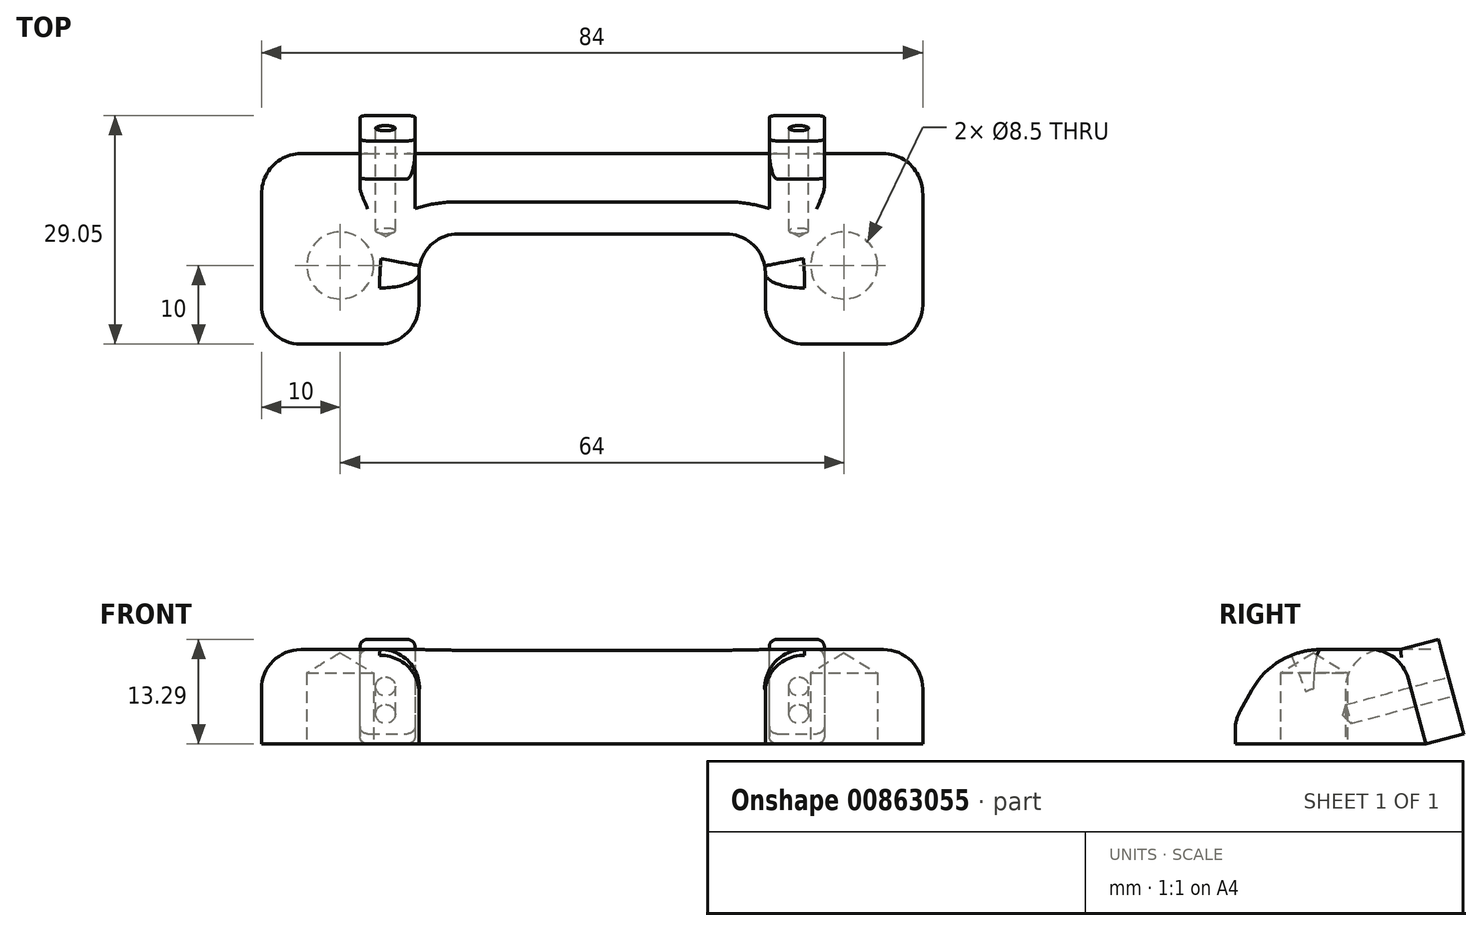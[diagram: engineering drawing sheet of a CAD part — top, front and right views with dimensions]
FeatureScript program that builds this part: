
annotation { "Feature Type Name" : "Feature", "Feature Type Description" : "" }
export const myFeature = defineFeature(function(context is Context, id is Id, definition is map)
    precondition{}
    {
        {
            var Q0;
            Q0=qCreatedBy(makeId("Top.planeOp"),FACE);
            var sketch = newSketch(context, id + "F0", { "sketchPlane" : qUnion([Q0])});
            skPoint(sketch, "E0", {"position": v(-32, 0) * mm});
            skPoint(sketch, "E1", {"position": v(32, 0) * mm});
            skLineSegment(sketch, "E2.bottom", {"start": v(-42, 8) * mm, "end": v(42, 8) * mm});
            skLineSegment(sketch, "E2.top", {"start": v(-42, -10) * mm, "end": v(42, -10) * mm});
            skLineSegment(sketch, "E2.left", {"start": v(-42, 8) * mm, "end": v(-42, -10) * mm});
            skLineSegment(sketch, "E2.right", {"start": v(42, 8) * mm, "end": v(42, -10) * mm});
            skLineSegment(sketch, "E3.top", {"start": v(-42, 11) * mm, "end": v(42, 11) * mm});
            skLineSegment(sketch, "E3.left", {"start": v(-42, 8) * mm, "end": v(-42, 11) * mm});
            skLineSegment(sketch, "E3.right", {"start": v(42, 8) * mm, "end": v(42, 11) * mm});
            skSolve(sketch);
        }
        {
            var Q0;
            Q0=makeQuery(id+"F0.imprint","IMPRINT",FACE,{"disambiguationData":[TD([[makeQuery(id+"F0.imprint","IMPRINT",EDGE,{"derivedFrom":sQuery(id+"F0.wireOp",EDGE,"MXNtf99J-OJbA-ETAj-UOV1-NQ5tLVOZiuJ5")}),-1.0]])]});
            var Q1;
            Q1=makeQuery(id+"F0.imprint","IMPRINT",FACE,{"disambiguationData":[TD([[makeQuery(id+"F0.imprint","IMPRINT",EDGE,{"derivedFrom":sQuery(id+"F0.wireOp",EDGE,"E2.bottom")}),1.0]])]});
            var Q2;
            Q2=makeQuery(id+"F0.imprint","IMPRINT",FACE,{"disambiguationData":[TD([[makeQuery(id+"F0.imprint","IMPRINT",EDGE,{"derivedFrom":sQuery(id+"F0.wireOp",EDGE,"MXNtf99J-OJbA-ETAj-UOV1-NQ5tLVOZiuJ5")}),1.0]])]});
            var Q3;
            Q3=makeQuery(id+"F0.imprint","IMPRINT",FACE,{"disambiguationData":[TD([[makeQuery(id+"F0.imprint","IMPRINT",EDGE,{"derivedFrom":sQuery(id+"F0.wireOp",EDGE,"yfzZAp0P-SpTb-lUpn-Zpsr-k5XURdNd0EC1")}),1.0]])]});
            var Q4;
            Q4=makeQuery(id+"F0.imprint","IMPRINT",FACE,{"disambiguationData":[TD([[makeQuery(id+"F0.imprint","IMPRINT",EDGE,{"derivedFrom":sQuery(id+"F0.wireOp",EDGE,"E2.top")}),1.0]])]});
            extrude(context, id + "F1", {"entities" : qUnion([Q0, Q1, Q2, Q3, Q4]), "depth" : 12 * mm, "offsetDistance" : 25 * mm});
        }
        {
            var Q0;
            Q0=sQuery(id+"F0.wireOp",VERTEX,"E0");
            var Q1;
            Q1=sQuery(id+"F0.wireOp",VERTEX,"E1");
            var Q2;
            Q2=makeQuery(id+"F1.opExtrude","SWEPT_BODY",BODY,{"disambiguationData":[OSD([sQuery(id+"F0.wireOp",EDGE,"E2.top"),sQuery(id+"F0.wireOp",EDGE,"E2.left"),sQuery(id+"F0.wireOp",EDGE,"E2.right"),sQuery(id+"F0.wireOp",EDGE,"E3.top"),sQuery(id+"F0.wireOp",EDGE,"E3.left"),sQuery(id+"F0.wireOp",EDGE,"E3.right")])]});
            hole(context, id + "F2", {"style" : HoleStyle.SIMPLE, "endStyle" : HoleEndStyle.BLIND, "oppositeDirection" : true, "holeDiameter" : 8.5 * mm, "majorDiameter" : 5 * mm, "holeDepth" : 9 * mm, "isTappedThrough" : true, "tappedDepth" : 12 * mm, "tapClearance" : 3, "locations" : qUnion([Q0, Q1]), "scope" : qUnion([Q2])});
        }
        {
            var Q0;
            Q0=makeQuery(id+"F1.opExtrude","SWEPT_FACE",FACE,{"disambiguationData":[OSD([sQuery(id+"F0.wireOp",EDGE,"E2.right"),sQuery(id+"F0.wireOp",EDGE,"E3.right")])]});
            var sketch = newSketch(context, id + "F3", { "sketchPlane" : qUnion([Q0])});
            skLineSegment(sketch, "E4", {"start": v(11, 0) * mm, "end": v(14.22, 0) * mm});
            skLineSegment(sketch, "E5", {"start": v(14.22, 0) * mm, "end": v(11, 12) * mm});
            skLineSegment(sketch, "E6", {"start": v(11, 12) * mm, "end": v(11, 0) * mm});
            skSolve(sketch);
        }
        {
            var Q0;
            Q0=makeQuery(id+"F3.imprint","IMPRINT",FACE,{"disambiguationData":[TD([[makeQuery(id+"F3.imprint","IMPRINT",EDGE,{"derivedFrom":sQuery(id+"F3.wireOp",EDGE,"E4")}),1.0]])]});
            var Q1;
            Q1=sQuery(id+"F0.wireOp",VERTEX,"E3.top.start");
            extrude(context, id + "F4", {"entities" : qUnion([Q0]), "operationType" : NewBodyOperationType.ADD, "endBound" : BoundingType.UP_TO_VERTEX, "oppositeDirection" : true, "depth" : 25 * mm, "endBoundEntityVertex" : qUnion([Q1]), "offsetDistance" : 25 * mm});
        }
        {
            var Q0;
            Q0=makeQuery(id+"F4.opExtrude","SWEPT_FACE",FACE,{"disambiguationData":[OSD([sQuery(id+"F3.wireOp",EDGE,"E5")])]});
            var sketch = newSketch(context, id + "F5", { "sketchPlane" : qUnion([Q0])});
            skLineSegment(sketch, "E7", {"start": v(-49.4, 2.58) * mm, "end": v(57.24, 2.58) * mm, "construction": true});
            skLineSegment(sketch, "E8", {"start": v(22.5, 8.74) * mm, "end": v(22.5, -3.68) * mm});
            skLineSegment(sketch, "E9", {"start": v(22.5, -3.68) * mm, "end": v(29.5, -3.68) * mm});
            skLineSegment(sketch, "E10", {"start": v(29.5, -3.68) * mm, "end": v(29.5, 8.74) * mm});
            skLineSegment(sketch, "E11", {"start": v(29.5, 8.74) * mm, "end": v(22.5, 8.74) * mm});
            skLineSegment(sketch, "E12", {"start": v(-29.5, 8.74) * mm, "end": v(-29.5, -3.68) * mm});
            skLineSegment(sketch, "E13", {"start": v(-29.5, -3.68) * mm, "end": v(-22.5, -3.68) * mm});
            skLineSegment(sketch, "E14", {"start": v(-22.5, -3.68) * mm, "end": v(-22.5, 8.74) * mm});
            skLineSegment(sketch, "E15", {"start": v(-22.5, 8.74) * mm, "end": v(-29.5, 8.74) * mm});
            skSolve(sketch);
        }
        {
            var Q0;
            Q0=makeQuery(id+"F5.imprint","IMPRINT",FACE,{"disambiguationData":[TD([[makeQuery(id+"F5.imprint","IMPRINT",EDGE,{"derivedFrom":sQuery(id+"F5.wireOp",EDGE,"E12")}),1.0]])]});
            var Q1;
            Q1=makeQuery(id+"F5.imprint","IMPRINT",FACE,{"disambiguationData":[TD([[makeQuery(id+"F5.imprint","IMPRINT",EDGE,{"derivedFrom":sQuery(id+"F5.wireOp",EDGE,"E8")}),1.0]])]});
            extrude(context, id + "F6", {"entities" : qUnion([Q0, Q1]), "operationType" : NewBodyOperationType.ADD, "depth" : 5 * mm, "offsetDistance" : 25 * mm});
        }
        {
            var Q0;
            Q0=makeQuery(id+"F6.opExtrude","CAP_FACE",FACE,{"disambiguationData":[OSD([sQuery(id+"F5.wireOp",EDGE,"E12"),sQuery(id+"F5.wireOp",EDGE,"E13"),sQuery(id+"F5.wireOp",EDGE,"E14"),sQuery(id+"F5.wireOp",EDGE,"E15")])],"isStart":false});
            var sketch = newSketch(context, id + "F7", { "sketchPlane" : qUnion([Q0])});
            skPoint(sketch, "E16", {"position": v(-26.25, 2.53) * mm});
            skPoint(sketch, "E16.positionSnap0", {"position": v(-29.5, 2.53) * mm});
            skSolve(sketch);
        }
        {
            var Q0;
            Q0=makeQuery(id+"F6.opExtrude","CAP_FACE",FACE,{"disambiguationData":[OSD([sQuery(id+"F5.wireOp",EDGE,"E8"),sQuery(id+"F5.wireOp",EDGE,"E9"),sQuery(id+"F5.wireOp",EDGE,"E10"),sQuery(id+"F5.wireOp",EDGE,"E11")])],"isStart":false});
            var sketch = newSketch(context, id + "F8", { "sketchPlane" : qUnion([Q0])});
            skPoint(sketch, "E17", {"position": v(26.25, 2.53) * mm});
            skPoint(sketch, "E17.positionSnap0", {"position": v(29.5, 2.53) * mm});
            skSolve(sketch);
        }
        {
            var Q0;
            Q0=sQuery(id+"F7.wireOp",VERTEX,"E16");
            var Q1;
            Q1=sQuery(id+"F8.wireOp",VERTEX,"E17");
            var Q2;
            Q2=makeQuery(id+"F1.opExtrude","SWEPT_BODY",BODY,{"disambiguationData":[OSD([sQuery(id+"F0.wireOp",EDGE,"E2.top"),sQuery(id+"F0.wireOp",EDGE,"E2.left"),sQuery(id+"F0.wireOp",EDGE,"E2.right"),sQuery(id+"F0.wireOp",EDGE,"E3.top"),sQuery(id+"F0.wireOp",EDGE,"E3.left"),sQuery(id+"F0.wireOp",EDGE,"E3.right")])]});
            hole(context, id + "F9", {"style" : HoleStyle.SIMPLE, "endStyle" : HoleEndStyle.BLIND, "standardTappedOrClearance" : lookupTablePath({ "standard" : "ISO", "engagement" : "75%", "pitch" : "0.5 mm", "size" : "M3", "type" : "Tapped" }), "standardBlindInLast" : lookupTablePath({ "standard" : "ISO", "engagement" : "75%", "pitch" : "0.5 mm", "size" : "M3", "type" : "Tapped" }), "holeDiameter" : 2.5 * mm, "majorDiameter" : 3 * mm, "showTappedDepth" : true, "holeDepth" : 13.5 * mm, "isTappedThrough" : true, "tappedDepth" : 12 * mm, "tapClearance" : 3, "locations" : qUnion([Q0, Q1]), "scope" : qUnion([Q2])});
        }
        {
            var Q0;
            Q0=makeQuery(id+"F0.imprint","IMPRINT",FACE,{"disambiguationData":[TD([[makeQuery(id+"F0.imprint","IMPRINT",EDGE,{"derivedFrom":sQuery(id+"F0.wireOp",EDGE,"E2.top")}),1.0]])]});
            var sketch = newSketch(context, id + "F10", { "sketchPlane" : qUnion([Q0])});
            skLineSegment(sketch, "E18", {"start": v(-22, -10) * mm, "end": v(-22, 4) * mm});
            skLineSegment(sketch, "E19", {"start": v(-22, 4) * mm, "end": v(22, 4) * mm});
            skLineSegment(sketch, "E20", {"start": v(22, 4) * mm, "end": v(22, -10) * mm});
            skLineSegment(sketch, "E21", {"start": v(-22, -10) * mm, "end": v(22, -10) * mm});
            skSolve(sketch);
        }
        {
            var Q0;
            Q0=makeQuery(id+"F10.imprint","IMPRINT",FACE,{"disambiguationData":[TD([[makeQuery(id+"F10.imprint","IMPRINT",EDGE,{"derivedFrom":sQuery(id+"F10.wireOp",EDGE,"E18")}),-1.0]])]});
            extrude(context, id + "F11", {"entities" : qUnion([Q0]), "operationType" : NewBodyOperationType.REMOVE, "depth" : 25 * mm, "offsetDistance" : 25 * mm});
        }
        {
            var Q0;
            {var subQ2=sQuery(id+"F0.wireOp",EDGE,"E2.top");Q0=makeQuery(id+"F11.boolean.opBoolean","SPLIT",EDGE,{"disambiguationData":[TD([makeQuery(id+"F11.opExtrude","SWEPT_FACE",FACE,{"disambiguationData":[OSD([sQuery(id+"F10.wireOp",EDGE,"E20")])]})])],"derivedFrom":makeQuery(id+"F1.opExtrude","CAP_EDGE",EDGE,{"disambiguationData":[OSD([subQ2])],"isStart":false})});}
            var Q1;
            {var subQ2=sQuery(id+"F0.wireOp",EDGE,"E2.top");Q1=makeQuery(id+"F11.boolean.opBoolean","SPLIT",EDGE,{"disambiguationData":[TD([makeQuery(id+"F11.opExtrude","SWEPT_FACE",FACE,{"disambiguationData":[OSD([sQuery(id+"F10.wireOp",EDGE,"E18")])]})])],"derivedFrom":makeQuery(id+"F1.opExtrude","CAP_EDGE",EDGE,{"disambiguationData":[OSD([subQ2])],"isStart":false})});}
            chamfer(context, id + "F12", {"entities" : qUnion([Q0, Q1]), "chamferType" : ChamferType.TWO_OFFSETS, "width1" : 5 * mm, "oppositeDirection" : false, "width2" : 9 * mm, "tangentPropagation" : true});
        }
        {
            var Q0;
            {var subQ0=sQuery(id+"F0.wireOp",EDGE,"E3.left");var subQ1=sQuery(id+"F0.wireOp",EDGE,"E2.left");var subQ2=sQuery(id+"F0.wireOp",EDGE,"E2.top");var subQ3=makeQuery(id+"F1.opExtrude","CAP_FACE",FACE,{"disambiguationData":[OSD([subQ2,subQ1,sQuery(id+"F0.wireOp",EDGE,"E2.right"),sQuery(id+"F0.wireOp",EDGE,"E3.top"),subQ0,sQuery(id+"F0.wireOp",EDGE,"E3.right")])],"isStart":false});Q0=makeQuery(id+"F12.opChamfer","BLEND_EDGE",EDGE,{"blendedFrom":[makeQuery(id+"F11.boolean.opBoolean","SPLIT",EDGE,{"disambiguationData":[TD([makeQuery(id+"F11.opExtrude","SWEPT_FACE",FACE,{"disambiguationData":[OSD([sQuery(id+"F10.wireOp",EDGE,"E18")])]})])],"derivedFrom":makeQuery(id+"F1.opExtrude","CAP_EDGE",EDGE,{"disambiguationData":[OSD([subQ2])],"isStart":false})}),subQ3],"blendedInto":[subQ3]});}
            var Q1;
            {var subQ0=sQuery(id+"F0.wireOp",EDGE,"E3.right");var subQ1=sQuery(id+"F0.wireOp",EDGE,"E2.right");var subQ2=sQuery(id+"F0.wireOp",EDGE,"E2.top");var subQ3=makeQuery(id+"F1.opExtrude","CAP_FACE",FACE,{"disambiguationData":[OSD([subQ2,sQuery(id+"F0.wireOp",EDGE,"E2.left"),subQ1,sQuery(id+"F0.wireOp",EDGE,"E3.top"),sQuery(id+"F0.wireOp",EDGE,"E3.left"),subQ0])],"isStart":false});Q1=makeQuery(id+"F12.opChamfer","BLEND_EDGE",EDGE,{"blendedFrom":[makeQuery(id+"F11.boolean.opBoolean","SPLIT",EDGE,{"disambiguationData":[TD([makeQuery(id+"F11.opExtrude","SWEPT_FACE",FACE,{"disambiguationData":[OSD([sQuery(id+"F10.wireOp",EDGE,"E20")])]})])],"derivedFrom":makeQuery(id+"F1.opExtrude","CAP_EDGE",EDGE,{"disambiguationData":[OSD([subQ2])],"isStart":false})}),subQ3],"blendedInto":[subQ3]});}
            fillet(context, id + "F13", {"entities" : qUnion([Q0, Q1]), "radius" : 10 * mm, "tangentPropagation" : true, "allowEdgeOverflow" : false});
        }
        {
            var Q0;
            {var subQ6=sQuery(id+"F0.wireOp",EDGE,"E2.top");var subQ10=makeQuery(id+"F11.opExtrude","SWEPT_FACE",FACE,{"disambiguationData":[OSD([sQuery(id+"F10.wireOp",EDGE,"E18")])]});var subQ11=makeQuery(id+"F1.opExtrude","SWEPT_FACE",FACE,{"disambiguationData":[OSD([subQ6])]});Q0=makeQuery(id+"F12.opChamfer","BLEND_EDGE",EDGE,{"blendedFrom":[makeQuery(id+"F11.boolean.opBoolean","SPLIT",EDGE,{"disambiguationData":[TD([subQ10])],"derivedFrom":makeQuery(id+"F1.opExtrude","CAP_EDGE",EDGE,{"disambiguationData":[OSD([subQ6])],"isStart":false})}),makeQuery(id+"F11.boolean.opBoolean","SPLIT",FACE,{"disambiguationData":[TD([subQ10])],"derivedFrom":subQ11})],"blendedInto":[makeQuery(id+"F11.boolean.opBoolean","SPLIT",FACE,{"disambiguationData":[TD([subQ10])],"derivedFrom":subQ11})]});}
            var Q1;
            {var subQ6=sQuery(id+"F0.wireOp",EDGE,"E2.top");var subQ10=makeQuery(id+"F11.opExtrude","SWEPT_FACE",FACE,{"disambiguationData":[OSD([sQuery(id+"F10.wireOp",EDGE,"E20")])]});var subQ11=makeQuery(id+"F1.opExtrude","SWEPT_FACE",FACE,{"disambiguationData":[OSD([subQ6])]});Q1=makeQuery(id+"F12.opChamfer","BLEND_EDGE",EDGE,{"blendedFrom":[makeQuery(id+"F11.boolean.opBoolean","SPLIT",EDGE,{"disambiguationData":[TD([subQ10])],"derivedFrom":makeQuery(id+"F1.opExtrude","CAP_EDGE",EDGE,{"disambiguationData":[OSD([subQ6])],"isStart":false})}),makeQuery(id+"F11.boolean.opBoolean","SPLIT",FACE,{"disambiguationData":[TD([subQ10])],"derivedFrom":subQ11})],"blendedInto":[makeQuery(id+"F11.boolean.opBoolean","SPLIT",FACE,{"disambiguationData":[TD([subQ10])],"derivedFrom":subQ11})]});}
            var Q2;
            {var subQ0=sQuery(id+"F3.wireOp",EDGE,"E6");var subQ1=sQuery(id+"F3.wireOp",EDGE,"E5");var subQ2=sQuery(id+"F0.wireOp",EDGE,"E3.right");var subQ3=sQuery(id+"F0.wireOp",EDGE,"E3.top");var subQ4=sQuery(id+"F0.wireOp",EDGE,"E2.right");Q2=makeQuery(id+"F6.boolean.opBoolean","SPLIT",EDGE,{"disambiguationData":[TD([makeQuery(id+"F6.opExtrude","SWEPT_FACE",FACE,{"disambiguationData":[OSD([sQuery(id+"F5.wireOp",EDGE,"E12")])]})])],"derivedFrom":makeQuery(id+"F4.boolean.opBoolean","MERGE",EDGE,{"derivedFrom":[makeQuery(id+"F1.opExtrude","CAP_EDGE",EDGE,{"disambiguationData":[OSD([subQ3])],"isStart":false}),makeQuery(id+"F4.opExtrude","SWEPT_EDGE",EDGE,{"disambiguationData":[OSD([subQ4,subQ2,subQ1,subQ0])]})]})});}
            var Q3;
            {var subQ0=sQuery(id+"F3.wireOp",EDGE,"E5");var subQ1=sQuery(id+"F0.wireOp",EDGE,"E3.right");var subQ2=sQuery(id+"F0.wireOp",EDGE,"E3.top");var subQ3=sQuery(id+"F0.wireOp",EDGE,"E2.right");Q3=makeQuery(id+"F6.boolean.opBoolean","SPLIT",EDGE,{"disambiguationData":[TD([makeQuery(id+"F6.opExtrude","SWEPT_FACE",FACE,{"disambiguationData":[OSD([sQuery(id+"F5.wireOp",EDGE,"E8")])]})])],"derivedFrom":makeQuery(id+"F4.boolean.opBoolean","MERGE",EDGE,{"derivedFrom":[makeQuery(id+"F1.opExtrude","CAP_EDGE",EDGE,{"disambiguationData":[OSD([subQ2])],"isStart":false}),makeQuery(id+"F4.opExtrude","SWEPT_EDGE",EDGE,{"disambiguationData":[OSD([subQ3,subQ1,subQ0,sQuery(id+"F3.wireOp",EDGE,"E6")])]})]})});}
            var Q4;
            {var subQ0=sQuery(id+"F3.wireOp",EDGE,"E6");var subQ1=sQuery(id+"F3.wireOp",EDGE,"E5");var subQ4=sQuery(id+"F0.wireOp",EDGE,"E3.right");var subQ5=sQuery(id+"F0.wireOp",EDGE,"E3.top");var subQ6=sQuery(id+"F0.wireOp",EDGE,"E2.right");Q4=makeQuery(id+"F6.boolean.opBoolean","SPLIT",EDGE,{"disambiguationData":[TD([makeQuery(id+"F6.opExtrude","SWEPT_FACE",FACE,{"disambiguationData":[OSD([sQuery(id+"F5.wireOp",EDGE,"E10")])]})])],"derivedFrom":makeQuery(id+"F4.boolean.opBoolean","MERGE",EDGE,{"derivedFrom":[makeQuery(id+"F1.opExtrude","CAP_EDGE",EDGE,{"disambiguationData":[OSD([subQ5])],"isStart":false}),makeQuery(id+"F4.opExtrude","SWEPT_EDGE",EDGE,{"disambiguationData":[OSD([subQ6,subQ4,subQ1,subQ0])]})]})});}
            fillet(context, id + "F14", {"entities" : qUnion([Q0, Q1, Q2, Q3, Q4]), "radius" : 5 * mm, "tangentPropagation" : true, "allowEdgeOverflow" : false});
        }
        {
            var Q0;
            {var subQ0=sQuery(id+"F3.wireOp",EDGE,"E6");var subQ1=sQuery(id+"F3.wireOp",EDGE,"E5");var subQ2=makeQuery(id+"F4.opExtrude","CAP_FACE",FACE,{"disambiguationData":[OSD([sQuery(id+"F3.wireOp",EDGE,"E4"),subQ1,subQ0])],"isStart":true});var subQ3=sQuery(id+"F0.wireOp",EDGE,"E3.right");var subQ4=sQuery(id+"F0.wireOp",EDGE,"E2.right");var subQ5=makeQuery(id+"F1.opExtrude","SWEPT_FACE",FACE,{"disambiguationData":[OSD([subQ4,subQ3])]});var subQ6=sQuery(id+"F0.wireOp",EDGE,"E3.top");Q0=makeQuery(id+"F14.opFillet","BLEND_EDGE",EDGE,{"blendedFrom":[makeQuery(id+"F6.boolean.opBoolean","SPLIT",EDGE,{"disambiguationData":[TD([makeQuery(id+"F6.opExtrude","SWEPT_FACE",FACE,{"disambiguationData":[OSD([sQuery(id+"F5.wireOp",EDGE,"E12")])]})])],"derivedFrom":makeQuery(id+"F4.boolean.opBoolean","MERGE",EDGE,{"derivedFrom":[makeQuery(id+"F1.opExtrude","CAP_EDGE",EDGE,{"disambiguationData":[OSD([subQ6])],"isStart":false}),makeQuery(id+"F4.opExtrude","SWEPT_EDGE",EDGE,{"disambiguationData":[OSD([subQ4,subQ3,subQ1,subQ0])]})]})}),makeQuery(id+"F4.boolean.opBoolean","MERGE",FACE,{"derivedFrom":[subQ5,subQ2]})],"blendedInto":[makeQuery(id+"F4.boolean.opBoolean","MERGE",FACE,{"derivedFrom":[subQ5,subQ2]})]});}
            var Q1;
            {var subQ0=sQuery(id+"F3.wireOp",EDGE,"E6");var subQ1=sQuery(id+"F3.wireOp",EDGE,"E5");var subQ2=makeQuery(id+"F4.opExtrude","CAP_FACE",FACE,{"disambiguationData":[OSD([sQuery(id+"F3.wireOp",EDGE,"E4"),subQ1,subQ0])],"isStart":false});var subQ3=sQuery(id+"F0.wireOp",EDGE,"E3.left");var subQ4=sQuery(id+"F0.wireOp",EDGE,"E2.left");var subQ5=makeQuery(id+"F1.opExtrude","SWEPT_FACE",FACE,{"disambiguationData":[OSD([subQ4,subQ3])]});var subQ6=sQuery(id+"F0.wireOp",EDGE,"E3.right");var subQ7=sQuery(id+"F0.wireOp",EDGE,"E3.top");var subQ8=sQuery(id+"F0.wireOp",EDGE,"E2.right");Q1=makeQuery(id+"F14.opFillet","BLEND_EDGE",EDGE,{"blendedFrom":[makeQuery(id+"F6.boolean.opBoolean","SPLIT",EDGE,{"disambiguationData":[TD([makeQuery(id+"F6.opExtrude","SWEPT_FACE",FACE,{"disambiguationData":[OSD([sQuery(id+"F5.wireOp",EDGE,"E10")])]})])],"derivedFrom":makeQuery(id+"F4.boolean.opBoolean","MERGE",EDGE,{"derivedFrom":[makeQuery(id+"F1.opExtrude","CAP_EDGE",EDGE,{"disambiguationData":[OSD([subQ7])],"isStart":false}),makeQuery(id+"F4.opExtrude","SWEPT_EDGE",EDGE,{"disambiguationData":[OSD([subQ8,subQ6,subQ1,subQ0])]})]})}),makeQuery(id+"F4.boolean.opBoolean","MERGE",FACE,{"derivedFrom":[subQ5,subQ2]})],"blendedInto":[makeQuery(id+"F4.boolean.opBoolean","MERGE",FACE,{"derivedFrom":[subQ5,subQ2]})]});}
            var Q2;
            Q2=makeQuery(id+"F11.boolean.opBoolean","COPY",EDGE,{"derivedFrom":makeQuery(id+"F11.opExtrude","SWEPT_EDGE",EDGE,{"disambiguationData":[OSD([sQuery(id+"F10.wireOp",EDGE,"E18"),sQuery(id+"F10.wireOp",EDGE,"E19")])]})});
            var Q3;
            Q3=makeQuery(id+"F11.boolean.opBoolean","COPY",EDGE,{"derivedFrom":makeQuery(id+"F11.opExtrude","SWEPT_EDGE",EDGE,{"disambiguationData":[OSD([sQuery(id+"F10.wireOp",EDGE,"E19"),sQuery(id+"F10.wireOp",EDGE,"E20")])]})});
            fillet(context, id + "F15", {"entities" : qUnion([Q0, Q1, Q2, Q3]), "radius" : 5 * mm, "tangentPropagation" : true, "allowEdgeOverflow" : false});
        }
        {
            var Q0;
            {var subQ0=makeQuery(id+"F11.opExtrude","SWEPT_FACE",FACE,{"disambiguationData":[OSD([sQuery(id+"F10.wireOp",EDGE,"E18")])]});var subQ1=sQuery(id+"F0.wireOp",EDGE,"E3.left");var subQ2=sQuery(id+"F0.wireOp",EDGE,"E2.left");var subQ3=sQuery(id+"F0.wireOp",EDGE,"E2.top");var subQ4=makeQuery(id+"F1.opExtrude","CAP_FACE",FACE,{"disambiguationData":[OSD([subQ3,subQ2,sQuery(id+"F0.wireOp",EDGE,"E2.right"),sQuery(id+"F0.wireOp",EDGE,"E3.top"),subQ1,sQuery(id+"F0.wireOp",EDGE,"E3.right")])],"isStart":false});Q0=makeQuery(id+"F13.opFillet","BLEND_EDGE",EDGE,{"blendedFrom":[makeQuery(id+"F12.opChamfer","BLEND_EDGE",EDGE,{"blendedFrom":[makeQuery(id+"F11.boolean.opBoolean","SPLIT",EDGE,{"disambiguationData":[TD([subQ0])],"derivedFrom":makeQuery(id+"F1.opExtrude","CAP_EDGE",EDGE,{"disambiguationData":[OSD([subQ3])],"isStart":false})}),subQ4],"blendedInto":[subQ4]}),makeQuery(id+"F11.boolean.opBoolean","COPY",FACE,{"derivedFrom":subQ0})],"blendedInto":[makeQuery(id+"F11.boolean.opBoolean","COPY",FACE,{"derivedFrom":subQ0})]});}
            fillet(context, id + "F16", {"entities" : qUnion([Q0]), "radius" : 5 * mm, "tangentPropagation" : true, "allowEdgeOverflow" : false});
        }
        {
            var Q0;
            Q0=makeQuery(id+"F6.opExtrude","SWEPT_EDGE",EDGE,{"disambiguationData":[OSD([sQuery(id+"F0.wireOp",EDGE,"E2.right"),sQuery(id+"F0.wireOp",EDGE,"E3.top"),sQuery(id+"F0.wireOp",EDGE,"E3.right"),sQuery(id+"F3.wireOp",EDGE,"E5"),sQuery(id+"F3.wireOp",EDGE,"E6"),sQuery(id+"F5.wireOp",EDGE,"E12"),sQuery(id+"F5.wireOp",EDGE,"E15")])]});
            var Q1;
            Q1=makeQuery(id+"F6.opExtrude","SWEPT_EDGE",EDGE,{"disambiguationData":[OSD([sQuery(id+"F0.wireOp",EDGE,"E2.right"),sQuery(id+"F0.wireOp",EDGE,"E3.top"),sQuery(id+"F0.wireOp",EDGE,"E3.right"),sQuery(id+"F3.wireOp",EDGE,"E5"),sQuery(id+"F3.wireOp",EDGE,"E6"),sQuery(id+"F5.wireOp",EDGE,"E14"),sQuery(id+"F5.wireOp",EDGE,"E15")])]});
            var Q2;
            Q2=makeQuery(id+"F6.opExtrude","SWEPT_EDGE",EDGE,{"disambiguationData":[OSD([sQuery(id+"F3.wireOp",EDGE,"E4"),sQuery(id+"F3.wireOp",EDGE,"E5"),sQuery(id+"F5.wireOp",EDGE,"E13"),sQuery(id+"F5.wireOp",EDGE,"E14")])]});
            var Q3;
            Q3=makeQuery(id+"F6.opExtrude","SWEPT_EDGE",EDGE,{"disambiguationData":[OSD([sQuery(id+"F3.wireOp",EDGE,"E4"),sQuery(id+"F3.wireOp",EDGE,"E5"),sQuery(id+"F5.wireOp",EDGE,"E12"),sQuery(id+"F5.wireOp",EDGE,"E13")])]});
            var Q4;
            Q4=makeQuery(id+"F6.opExtrude","SWEPT_EDGE",EDGE,{"disambiguationData":[OSD([sQuery(id+"F3.wireOp",EDGE,"E4"),sQuery(id+"F3.wireOp",EDGE,"E5"),sQuery(id+"F5.wireOp",EDGE,"E8"),sQuery(id+"F5.wireOp",EDGE,"E9")])]});
            var Q5;
            Q5=makeQuery(id+"F6.opExtrude","SWEPT_EDGE",EDGE,{"disambiguationData":[OSD([sQuery(id+"F3.wireOp",EDGE,"E4"),sQuery(id+"F3.wireOp",EDGE,"E5"),sQuery(id+"F5.wireOp",EDGE,"E9"),sQuery(id+"F5.wireOp",EDGE,"E10")])]});
            var Q6;
            Q6=makeQuery(id+"F6.opExtrude","SWEPT_EDGE",EDGE,{"disambiguationData":[OSD([sQuery(id+"F0.wireOp",EDGE,"E2.right"),sQuery(id+"F0.wireOp",EDGE,"E3.top"),sQuery(id+"F0.wireOp",EDGE,"E3.right"),sQuery(id+"F3.wireOp",EDGE,"E5"),sQuery(id+"F3.wireOp",EDGE,"E6"),sQuery(id+"F5.wireOp",EDGE,"E10"),sQuery(id+"F5.wireOp",EDGE,"E11")])]});
            var Q7;
            Q7=makeQuery(id+"F6.opExtrude","SWEPT_EDGE",EDGE,{"disambiguationData":[OSD([sQuery(id+"F0.wireOp",EDGE,"E2.right"),sQuery(id+"F0.wireOp",EDGE,"E3.top"),sQuery(id+"F0.wireOp",EDGE,"E3.right"),sQuery(id+"F3.wireOp",EDGE,"E5"),sQuery(id+"F3.wireOp",EDGE,"E6"),sQuery(id+"F5.wireOp",EDGE,"E8"),sQuery(id+"F5.wireOp",EDGE,"E11")])]});
            var Q8;
            Q8=makeQuery(id+"F14.opFillet","TWEAK_EDGE",EDGE,{"derivedFrom":[makeQuery(id+"F6.opExtrude","CAP_VERTEX",VERTEX,{"disambiguationData":[OSD([sQuery(id+"F0.wireOp",EDGE,"E2.right"),sQuery(id+"F0.wireOp",EDGE,"E3.top"),sQuery(id+"F0.wireOp",EDGE,"E3.right"),sQuery(id+"F3.wireOp",EDGE,"E5"),sQuery(id+"F3.wireOp",EDGE,"E6"),sQuery(id+"F5.wireOp",EDGE,"E10"),sQuery(id+"F5.wireOp",EDGE,"E11")])],"isStart":true})]});
            var Q9;
            Q9=makeQuery(id+"F14.opFillet","TWEAK_EDGE",EDGE,{"derivedFrom":[makeQuery(id+"F6.opExtrude","CAP_VERTEX",VERTEX,{"disambiguationData":[OSD([sQuery(id+"F0.wireOp",EDGE,"E2.right"),sQuery(id+"F0.wireOp",EDGE,"E3.top"),sQuery(id+"F0.wireOp",EDGE,"E3.right"),sQuery(id+"F3.wireOp",EDGE,"E5"),sQuery(id+"F3.wireOp",EDGE,"E6"),sQuery(id+"F5.wireOp",EDGE,"E12"),sQuery(id+"F5.wireOp",EDGE,"E15")])],"isStart":true})]});
            fillet(context, id + "F17", {"entities" : qUnion([Q0, Q1, Q2, Q3, Q4, Q5, Q6, Q7, Q8, Q9]), "radius" : 1 * mm, "tangentPropagation" : true, "allowEdgeOverflow" : false});
        }
    });
